# Revit family: 0066631-WM
name_source: partatom
category: Lighting Fixtures
revit_build: Autodesk Revit 2017 (Build: 20190507_1515(x64)
units: mm (PartAtom-declared; Revit-internal decimal feet)

## family parameters
Cut with Voids When Loaded = No
Host = Face
Light Source = Yes
OmniClass Number = 23.80.70.00
OmniClass Title = Lighting
Part Type = Normal
Room Calculation Point = No
Round Connector Dimension = Use Diameter
Shared = No

## types (1)
- 0066631 SKS M 5-12KLM NW NR17 I 9022
    Apparent Load = 103 VA
    Assembly Code = D5020200
    AssetType = Fixed
    ClassificationName = Uniclass2015
    ClassificationValue = EF_70_80
    Color Filter = 16777215
    Cost = 0 $
    Default Elevation = 1219 mm
    Description = The Skyline Street family is dedicated for road lighting applications. Light distribution: NR17 - Narrow Road, color temperature: 4000K , total system power: 103W, total fixture output: 13038lm, luminaire efficacy: 127lm/W, LOR: 100%, colour rendering index: 70, LED Chromaticity: 5 step MacAdam ellipse tolerance, lifetime: 100000 hours at L90B50 @ 50°C, energy class: A++, A+, A, operating voltage: 220-240V / 50-60Hz, electronic driver, Without Controls, power factor: min. 0.9, electrical protection: Class I, Ingress protection rating: IP66, Impact resistance: IK08, dimensions: 625x290x105mm, weight: 7 kg, for 42-60mm side entry or post top installation with +/-15° adjustability, the housing is made of Die Cast Aluminium in RAL9022 color combined with tempered flat glass cover.
    Dimming Lamp Color Temperature Shift = <None>
    DocumentationLiterature = http://www.sylvania-lighting.com
    DurationUnit = hours
    ElectricShockClassification = 127
    Emit Shape Visible in Rendering = No
    Emit from Rectangle Length = 1219 mm
    Emit from Rectangle Width = 610 mm
    ExpectedLife = 50000
    Height = 100 mm  [stored 0.328084 ft]
    IfcExportAs = Class I
    IfcExportType = IfcLightFixtureType
    ImpactProtectionIndex = IfcLightFixtureType
    IngressProtection = IfcLightFixtureType
    InputNominalFrequency = 4000
    InputVoltage = 0
    LampColourRenderingIndex = 16500
    LampColourTemperature = LED
    LampMacAdamStep = 70
    LampNominalLuminous = 4000 K
    Length = 625 mm  [stored 2.05052 ft]
    LightOutputRatio = LED
    LuminaireType = 0
    Manufacturer = Feilo Sylvania
    ManufacturerName = Feilo Sylvania
    Material = Feilo Sylvania
    Material_1_FEILO = <By Category>
    Material_2_FEILO = <By Category>
    Material_3_FEILO = <By Category>
    Material_4_FEILO = <By Category>
    Model = Skyline Street M 5-12klm NW NR17 I 9022
    ModelNumber = 0066631
    ModelReference = Skyline Street M 5-12klm NW NR17 I 9022
    Name = Skyline Street M 5-12klm NW NR17 I 9022
    NominalDepth = 0 mm  [stored 0 ft]
    NominalHeight = 0 mm  [stored 0 ft]
    NominalLength = 290 mm  [stored 0.951444 ft]
    Photometric Web File = 0066631.ies
    PowerConsumption = Lighting
    PowerFactor = 0
    Tilt Angle = 90.00°
    Type Image = <None>
    TypeName = Skyline Street M 5-12klm NW NR17 I 9022
    URL = http://www.sylvania-lighting.com
    Voltage = 0 V
    WarrantyDescription = http://www.sylvania-lighting.com

note: [stored X ft] marks values corroborated as IEEE doubles in the binary element streams (Revit-internal decimal feet)

## geometry (parser evidence)
native form markers: Sweep x3
no freeform markers — native parametric forms only
